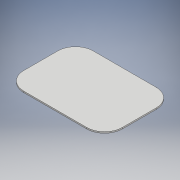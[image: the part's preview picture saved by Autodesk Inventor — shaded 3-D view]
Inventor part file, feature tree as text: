
AUTODESK INVENTOR PART (.ipt)
format: ipt  version: 2018 (Build 220112000, 112)  size: 100,352 bytes
history: native  units: mm
features: extrude x1, sketch x1
ambient origin geometry x8: Origin, YZ Plane, XZ Plane, XY Plane, X Axis, Y Axis, Z Axis, Center Point
bodies: Solid1 (feature_tree)
feature tree (2):
  extrude  "Extrusion1"  Depth=98.0mm
  sketch  "Sketch1"  dims[d0=139.0mm d1=98.0mm d2=25.0mm d3=2.0mm d4=0.0mm]
